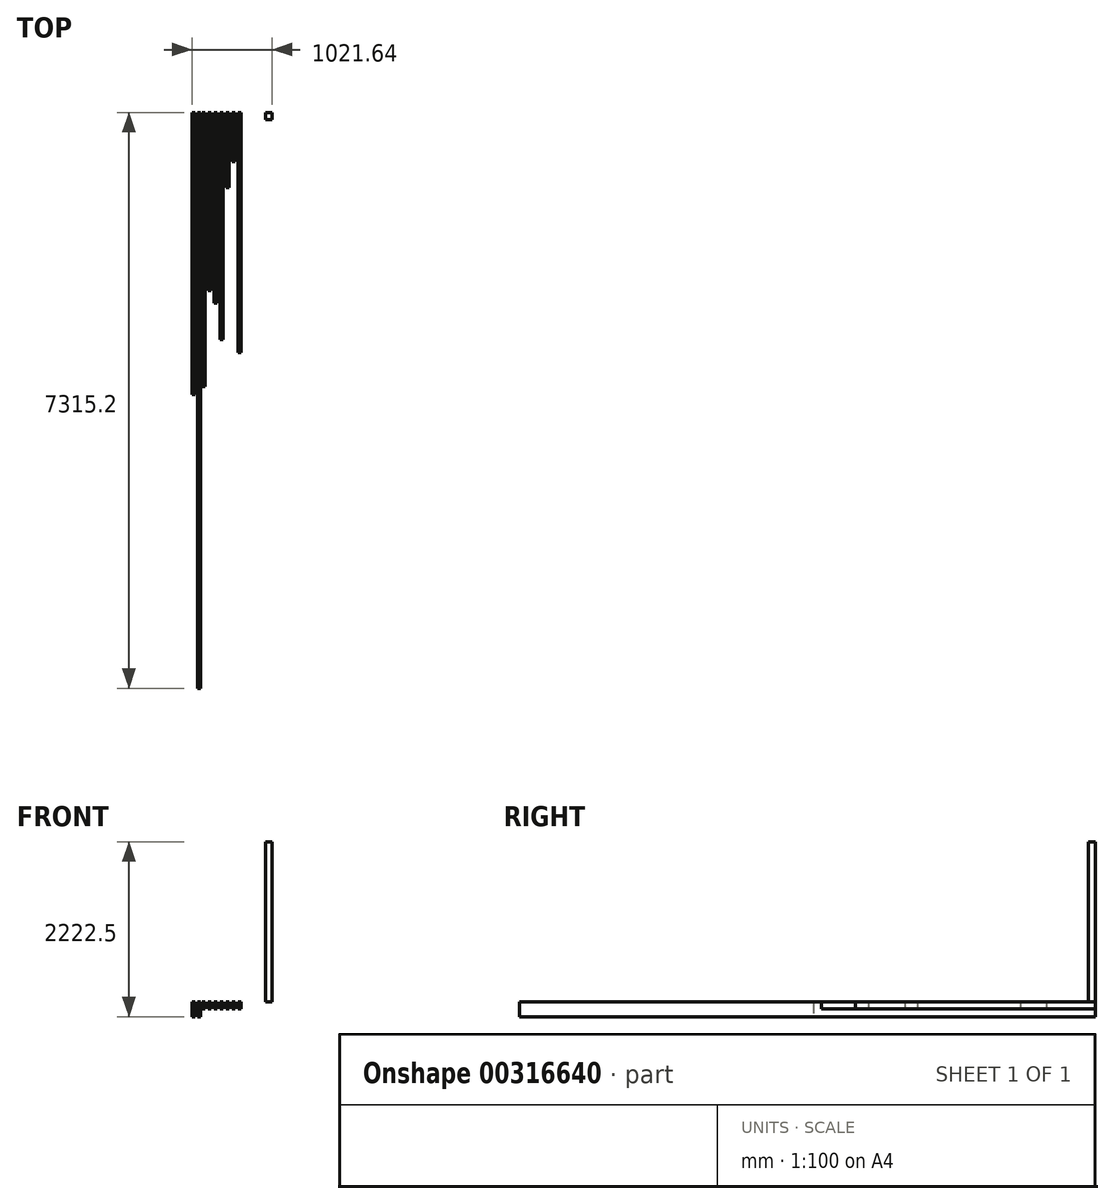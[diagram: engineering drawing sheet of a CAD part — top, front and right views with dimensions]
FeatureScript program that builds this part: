
annotation { "Feature Type Name" : "Feature", "Feature Type Description" : "" }
export const myFeature = defineFeature(function(context is Context, id is Id, definition is map)
    precondition{}
    {
        {
            var Q0;
            Q0=qCreatedBy(makeId("Front.planeOp"),FACE);
            var sketch = newSketch(context, id + "F0", { "sketchPlane" : qUnion([Q0])});
            skLineSegment(sketch, "E0.bottom", {"start": v(-61.8, 0) * mm, "end": v(-23.7, 0) * mm});
            skLineSegment(sketch, "E0.top", {"start": v(-61.8, -190.5) * mm, "end": v(-23.7, -190.5) * mm});
            skLineSegment(sketch, "E0.left", {"start": v(-61.8, 0) * mm, "end": v(-61.8, -190.5) * mm});
            skLineSegment(sketch, "E0.right", {"start": v(-23.7, 0) * mm, "end": v(-23.7, -190.5) * mm});
            skSolve(sketch);
        }
        {
            var Q0;
            Q0=makeQuery(id+"F0.imprint","IMPRINT",FACE,{"disambiguationData":[TD([[makeQuery(id+"F0.imprint","IMPRINT",EDGE,{"derivedFrom":sQuery(id+"F0.wireOp",EDGE,"E0.bottom")}),-1.0]])]});
            extrude(context, id + "F1", {"entities" : qUnion([Q0]), "depth" : 3581.4 * mm});
        }
        {
            var Q0;
            Q0=qCreatedBy(makeId("Front.planeOp"),FACE);
            var sketch = newSketch(context, id + "F2", { "sketchPlane" : qUnion([Q0])});
            skLineSegment(sketch, "E1.bottom", {"start": v(11.74, 0) * mm, "end": v(49.84, 0) * mm});
            skLineSegment(sketch, "E1.top", {"start": v(11.74, -190.5) * mm, "end": v(49.84, -190.5) * mm});
            skLineSegment(sketch, "E1.left", {"start": v(11.74, 0) * mm, "end": v(11.74, -190.5) * mm});
            skLineSegment(sketch, "E1.right", {"start": v(49.84, 0) * mm, "end": v(49.84, -190.5) * mm});
            skSolve(sketch);
        }
        {
            var Q0;
            Q0 = qSketchRegion(id + "F2", true);
            extrude(context, id + "F3", {"entities" : qUnion([Q0]), "depth" : 7315.2 * mm});
        }
        {
            var Q0;
            Q0=qCreatedBy(makeId("Front.planeOp"),FACE);
            var sketch = newSketch(context, id + "F4", { "sketchPlane" : qUnion([Q0])});
            skLineSegment(sketch, "E2.bottom", {"start": v(65.94, 0) * mm, "end": v(104.04, 0) * mm});
            skLineSegment(sketch, "E2.top", {"start": v(65.94, -88.9) * mm, "end": v(104.04, -88.9) * mm});
            skLineSegment(sketch, "E2.left", {"start": v(65.94, 0) * mm, "end": v(65.94, -88.9) * mm});
            skLineSegment(sketch, "E2.right", {"start": v(104.04, 0) * mm, "end": v(104.04, -88.9) * mm});
            skLineSegment(sketch, "E3.1.0.0", {"start": v(180.24, 0) * mm, "end": v(180.24, -88.9) * mm});
            skLineSegment(sketch, "E3.1.0.1", {"start": v(142.14, -88.9) * mm, "end": v(180.24, -88.9) * mm});
            skLineSegment(sketch, "E3.1.0.2", {"start": v(142.14, 0) * mm, "end": v(142.14, -88.9) * mm});
            skLineSegment(sketch, "E3.1.0.3", {"start": v(142.14, 0) * mm, "end": v(180.24, 0) * mm});
            skLineSegment(sketch, "E3.2.0.0", {"start": v(256.44, 0) * mm, "end": v(256.44, -88.9) * mm});
            skLineSegment(sketch, "E3.2.0.1", {"start": v(218.34, -88.9) * mm, "end": v(256.44, -88.9) * mm});
            skLineSegment(sketch, "E3.2.0.2", {"start": v(218.34, 0) * mm, "end": v(218.34, -88.9) * mm});
            skLineSegment(sketch, "E3.2.0.3", {"start": v(218.34, 0) * mm, "end": v(256.44, 0) * mm});
            skLineSegment(sketch, "E3.3.0.0", {"start": v(332.64, 0) * mm, "end": v(332.64, -88.9) * mm});
            skLineSegment(sketch, "E3.3.0.1", {"start": v(294.54, -88.9) * mm, "end": v(332.64, -88.9) * mm});
            skLineSegment(sketch, "E3.3.0.2", {"start": v(294.54, 0) * mm, "end": v(294.54, -88.9) * mm});
            skLineSegment(sketch, "E3.3.0.3", {"start": v(294.54, 0) * mm, "end": v(332.64, 0) * mm});
            skLineSegment(sketch, "E3.4.0.0", {"start": v(408.84, 0) * mm, "end": v(408.84, -88.9) * mm});
            skLineSegment(sketch, "E3.4.0.1", {"start": v(370.74, -88.9) * mm, "end": v(408.84, -88.9) * mm});
            skLineSegment(sketch, "E3.4.0.2", {"start": v(370.74, 0) * mm, "end": v(370.74, -88.9) * mm});
            skLineSegment(sketch, "E3.4.0.3", {"start": v(370.74, 0) * mm, "end": v(408.84, 0) * mm});
            skLineSegment(sketch, "E3.5.0.0", {"start": v(485.04, 0) * mm, "end": v(485.04, -88.9) * mm});
            skLineSegment(sketch, "E3.5.0.1", {"start": v(446.94, -88.9) * mm, "end": v(485.04, -88.9) * mm});
            skLineSegment(sketch, "E3.5.0.2", {"start": v(446.94, 0) * mm, "end": v(446.94, -88.9) * mm});
            skLineSegment(sketch, "E3.5.0.3", {"start": v(446.94, 0) * mm, "end": v(485.04, 0) * mm});
            skLineSegment(sketch, "E3.6.0.0", {"start": v(561.24, 0) * mm, "end": v(561.24, -88.9) * mm});
            skLineSegment(sketch, "E3.6.0.1", {"start": v(523.14, -88.9) * mm, "end": v(561.24, -88.9) * mm});
            skLineSegment(sketch, "E3.6.0.2", {"start": v(523.14, 0) * mm, "end": v(523.14, -88.9) * mm});
            skLineSegment(sketch, "E3.6.0.3", {"start": v(523.14, 0) * mm, "end": v(561.24, 0) * mm});
            skLineSegment(sketch, "E3.7.0.0", {"start": v(637.44, 0) * mm, "end": v(637.44, -88.9) * mm});
            skLineSegment(sketch, "E3.7.0.1", {"start": v(599.34, -88.9) * mm, "end": v(637.44, -88.9) * mm});
            skLineSegment(sketch, "E3.7.0.2", {"start": v(599.34, 0) * mm, "end": v(599.34, -88.9) * mm});
            skLineSegment(sketch, "E3.7.0.3", {"start": v(599.34, 0) * mm, "end": v(637.44, 0) * mm});
            skLineSegment(sketch, "E3.8.0.0", {"start": v(713.64, 0) * mm, "end": v(713.64, -88.9) * mm});
            skLineSegment(sketch, "E3.8.0.1", {"start": v(675.54, -88.9) * mm, "end": v(713.64, -88.9) * mm});
            skLineSegment(sketch, "E3.8.0.2", {"start": v(675.54, 0) * mm, "end": v(675.54, -88.9) * mm});
            skLineSegment(sketch, "E3.8.0.3", {"start": v(675.54, 0) * mm, "end": v(713.64, 0) * mm});
            skLineSegment(sketch, "E3.9.0.0", {"start": v(789.84, 0) * mm, "end": v(789.84, -88.9) * mm});
            skLineSegment(sketch, "E3.9.0.1", {"start": v(751.74, -88.9) * mm, "end": v(789.84, -88.9) * mm});
            skLineSegment(sketch, "E3.9.0.2", {"start": v(751.74, 0) * mm, "end": v(751.74, -88.9) * mm});
            skLineSegment(sketch, "E3.9.0.3", {"start": v(751.74, 0) * mm, "end": v(789.84, 0) * mm});
            skLineSegment(sketch, "E3.direction1", {"start": v(104.04, -88.9) * mm, "end": v(180.24, -88.9) * mm, "construction": true});
            skSolve(sketch);
        }
        {
            var Q0;
            Q0=makeQuery(id+"F4.imprint","IMPRINT",FACE,{"disambiguationData":[TD([[makeQuery(id+"F4.imprint","IMPRINT",EDGE,{"derivedFrom":sQuery(id+"F4.wireOp",EDGE,"E2.bottom")}),-1.0]])]});
            extrude(context, id + "F5", {"entities" : qUnion([Q0]), "depth" : 3479.8 * mm});
        }
        {
            var Q0;
            Q0=makeQuery(id+"F4.imprint","IMPRINT",FACE,{"disambiguationData":[TD([[makeQuery(id+"F4.imprint","IMPRINT",EDGE,{"derivedFrom":sQuery(id+"F4.wireOp",EDGE,"E3.1.0.0")}),-1.0]])]});
            extrude(context, id + "F6", {"entities" : qUnion([Q0]), "depth" : 2260.6 * mm});
        }
        {
            var Q0;
            Q0=makeQuery(id+"F4.imprint","IMPRINT",FACE,{"disambiguationData":[TD([[makeQuery(id+"F4.imprint","IMPRINT",EDGE,{"derivedFrom":sQuery(id+"F4.wireOp",EDGE,"E3.2.0.0")}),-1.0]])]});
            extrude(context, id + "F7", {"entities" : qUnion([Q0]), "depth" : 2419.35 * mm});
        }
        {
            var Q0;
            Q0=makeQuery(id+"F4.imprint","IMPRINT",FACE,{"disambiguationData":[TD([[makeQuery(id+"F4.imprint","IMPRINT",EDGE,{"derivedFrom":sQuery(id+"F4.wireOp",EDGE,"E3.3.0.0")}),-1.0]])]});
            extrude(context, id + "F8", {"entities" : qUnion([Q0]), "depth" : 2882.9 * mm});
        }
        {
            var Q0;
            Q0=makeQuery(id+"F4.imprint","IMPRINT",FACE,{"disambiguationData":[TD([[makeQuery(id+"F4.imprint","IMPRINT",EDGE,{"derivedFrom":sQuery(id+"F4.wireOp",EDGE,"E3.4.0.0")}),-1.0]])]});
            extrude(context, id + "F9", {"entities" : qUnion([Q0]), "depth" : 952.5 * mm});
        }
        {
            var Q0;
            Q0=makeQuery(id+"F4.imprint","IMPRINT",FACE,{"disambiguationData":[TD([[makeQuery(id+"F4.imprint","IMPRINT",EDGE,{"derivedFrom":sQuery(id+"F4.wireOp",EDGE,"E3.5.0.0")}),-1.0]])]});
            extrude(context, id + "F10", {"entities" : qUnion([Q0]), "depth" : 622.3 * mm});
        }
        {
            var Q0;
            Q0=qCreatedBy(makeId("Top.planeOp"),FACE);
            var sketch = newSketch(context, id + "F11", { "sketchPlane" : qUnion([Q0])});
            skLineSegment(sketch, "E4.bottom", {"start": v(870.94, 0) * mm, "end": v(959.84, 0) * mm});
            skLineSegment(sketch, "E4.top", {"start": v(870.94, -88.9) * mm, "end": v(959.84, -88.9) * mm});
            skLineSegment(sketch, "E4.left", {"start": v(870.94, 0) * mm, "end": v(870.94, -88.9) * mm});
            skLineSegment(sketch, "E4.right", {"start": v(959.84, 0) * mm, "end": v(959.84, -88.9) * mm});
            skSolve(sketch);
        }
        {
            var Q0;
            Q0=makeQuery(id+"F11.imprint","IMPRINT",FACE,{"disambiguationData":[TD([[makeQuery(id+"F11.imprint","IMPRINT",EDGE,{"derivedFrom":sQuery(id+"F11.wireOp",EDGE,"E4.bottom")}),-1.0]])]});
            extrude(context, id + "F12", {"entities" : qUnion([Q0]), "depth" : 2032 * mm});
        }
        {
            var Q0;
            Q0=makeQuery(id+"F4.imprint","IMPRINT",FACE,{"disambiguationData":[TD([[makeQuery(id+"F4.imprint","IMPRINT",EDGE,{"derivedFrom":sQuery(id+"F4.wireOp",EDGE,"E3.6.0.0")}),-1.0]])]});
            extrude(context, id + "F13", {"entities" : qUnion([Q0]), "depth" : 3048 * mm});
        }
    });
